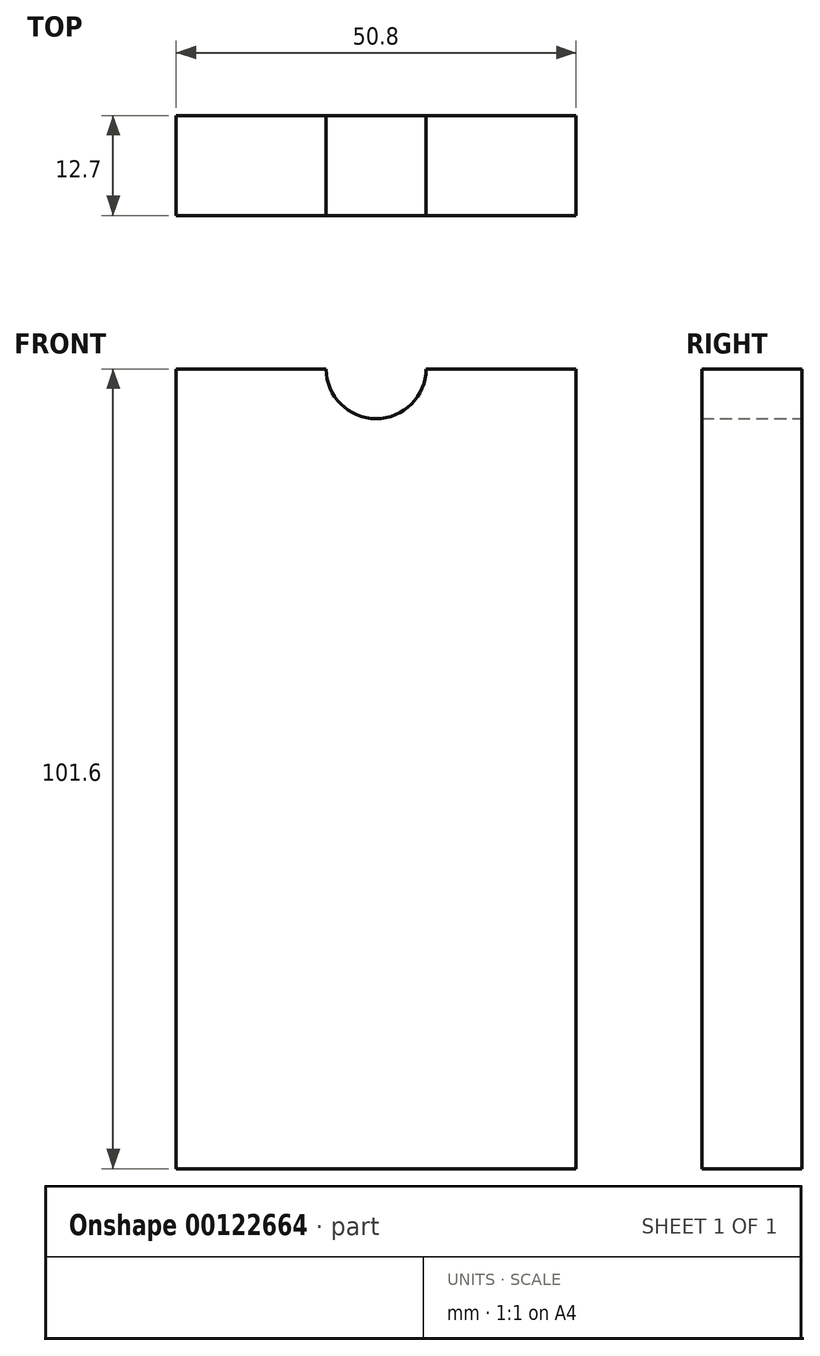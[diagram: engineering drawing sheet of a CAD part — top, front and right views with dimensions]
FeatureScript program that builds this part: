
annotation { "Feature Type Name" : "Feature", "Feature Type Description" : "" }
export const myFeature = defineFeature(function(context is Context, id is Id, definition is map)
    precondition{}
    {
        {
            var Q0;
            Q0=qCreatedBy(makeId("Front.planeOp"),FACE);
            var sketch = newSketch(context, id + "F0", { "sketchPlane" : qUnion([Q0])});
            skLineSegment(sketch, "E0.top", {"start": v(0, -101.6) * mm, "end": v(50.8, -101.6) * mm});
            skLineSegment(sketch, "E0.left", {"start": v(0, 0) * mm, "end": v(0, -101.6) * mm});
            skLineSegment(sketch, "E0.right", {"start": v(50.8, 0) * mm, "end": v(50.8, -101.6) * mm});
            skArc(sketch, "E1", {"start": v(19.05, 0) * mm, "mid": v(25.4, -6.33) * mm, "end": v(31.75, 0) * mm});
            skLineSegment(sketch, "E2", {"start": v(31.75, 0) * mm, "end": v(50.8, 0) * mm});
            skLineSegment(sketch, "E3", {"start": v(19.05, 0) * mm, "end": v(0, 0) * mm});
            skSolve(sketch);
        }
        {
            var Q0;
            Q0=makeQuery(id+"F0.imprint","IMPRINT",FACE,{"disambiguationData":[TD([[makeQuery(id+"F0.imprint","IMPRINT",EDGE,{"derivedFrom":sQuery(id+"F0.wireOp",EDGE,"E0.top")}),1.0]])]});
            extrude(context, id + "F1", {"entities" : qUnion([Q0]), "depth" : 12.7 * mm});
        }
    });
